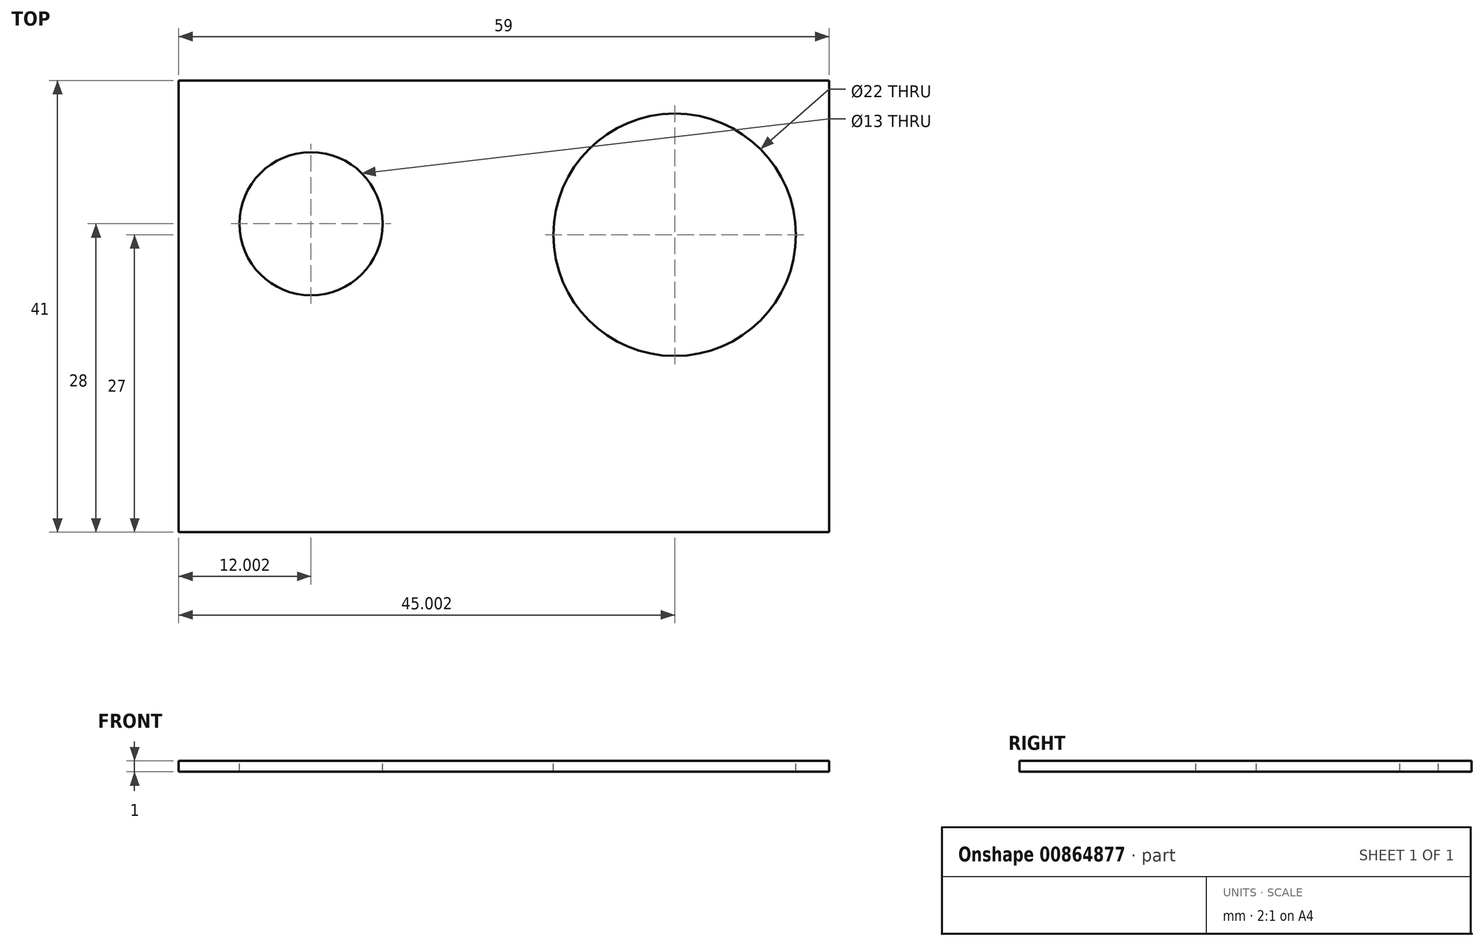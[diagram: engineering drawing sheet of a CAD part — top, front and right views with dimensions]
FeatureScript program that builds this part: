
annotation { "Feature Type Name" : "Feature", "Feature Type Description" : "" }
export const myFeature = defineFeature(function(context is Context, id is Id, definition is map)
    precondition{}
    {
        {
            var Q0;
            Q0=qCreatedBy(makeId("Top.planeOp"),FACE);
            var sketch = newSketch(context, id + "F0", { "sketchPlane" : qUnion([Q0])});
            skLineSegment(sketch, "E0.bottom", {"start": v(-60.83, 14.24) * mm, "end": v(-1.83, 14.24) * mm});
            skLineSegment(sketch, "E0.top", {"start": v(-60.83, -26.76) * mm, "end": v(-1.83, -26.76) * mm});
            skLineSegment(sketch, "E0.left", {"start": v(-60.83, 14.24) * mm, "end": v(-60.83, -26.76) * mm});
            skLineSegment(sketch, "E0.right", {"start": v(-1.83, 14.24) * mm, "end": v(-1.83, -26.76) * mm});
            skSolve(sketch);
        }
        {
            var Q0;
            Q0 = qSketchRegion(id + "F0", true);
            extrude(context, id + "F1", {"entities" : qUnion([Q0]), "depth" : 1 * mm, "offsetDistance" : 25 * mm});
        }
        {
            var Q0;
            Q0=makeQuery(id+"F1.opExtrude","CAP_FACE",FACE,{"disambiguationData":[OSD([sQuery(id+"F0.wireOp",EDGE,"E0.bottom"),sQuery(id+"F0.wireOp",EDGE,"E0.top"),sQuery(id+"F0.wireOp",EDGE,"E0.left"),sQuery(id+"F0.wireOp",EDGE,"E0.right")])],"isStart":false});
            var sketch = newSketch(context, id + "F2", { "sketchPlane" : qUnion([Q0])});
            skCircle(sketch, "E1", {"center": v(-15.83, 0.24) * mm, "radius": 11 * mm});
            skSolve(sketch);
        }
        {
            var Q0;
            Q0 = qSketchRegion(id + "F2", true);
            extrude(context, id + "F3", {"entities" : qUnion([Q0]), "operationType" : NewBodyOperationType.REMOVE, "oppositeDirection" : true, "depth" : 25 * mm, "offsetDistance" : 25 * mm});
        }
        {
            var Q0;
            Q0=makeQuery(id+"F1.opExtrude","CAP_FACE",FACE,{"disambiguationData":[OSD([sQuery(id+"F0.wireOp",EDGE,"E0.bottom"),sQuery(id+"F0.wireOp",EDGE,"E0.top"),sQuery(id+"F0.wireOp",EDGE,"E0.left"),sQuery(id+"F0.wireOp",EDGE,"E0.right")])],"isStart":false});
            var sketch = newSketch(context, id + "F4", { "sketchPlane" : qUnion([Q0])});
            skCircle(sketch, "E2", {"center": v(-48.83, 1.24) * mm, "radius": 6.5 * mm});
            skSolve(sketch);
        }
        {
            var Q0;
            Q0 = qSketchRegion(id + "F4", true);
            extrude(context, id + "F5", {"entities" : qUnion([Q0]), "operationType" : NewBodyOperationType.REMOVE, "oppositeDirection" : true, "depth" : 25 * mm, "offsetDistance" : 25 * mm});
        }
    });
